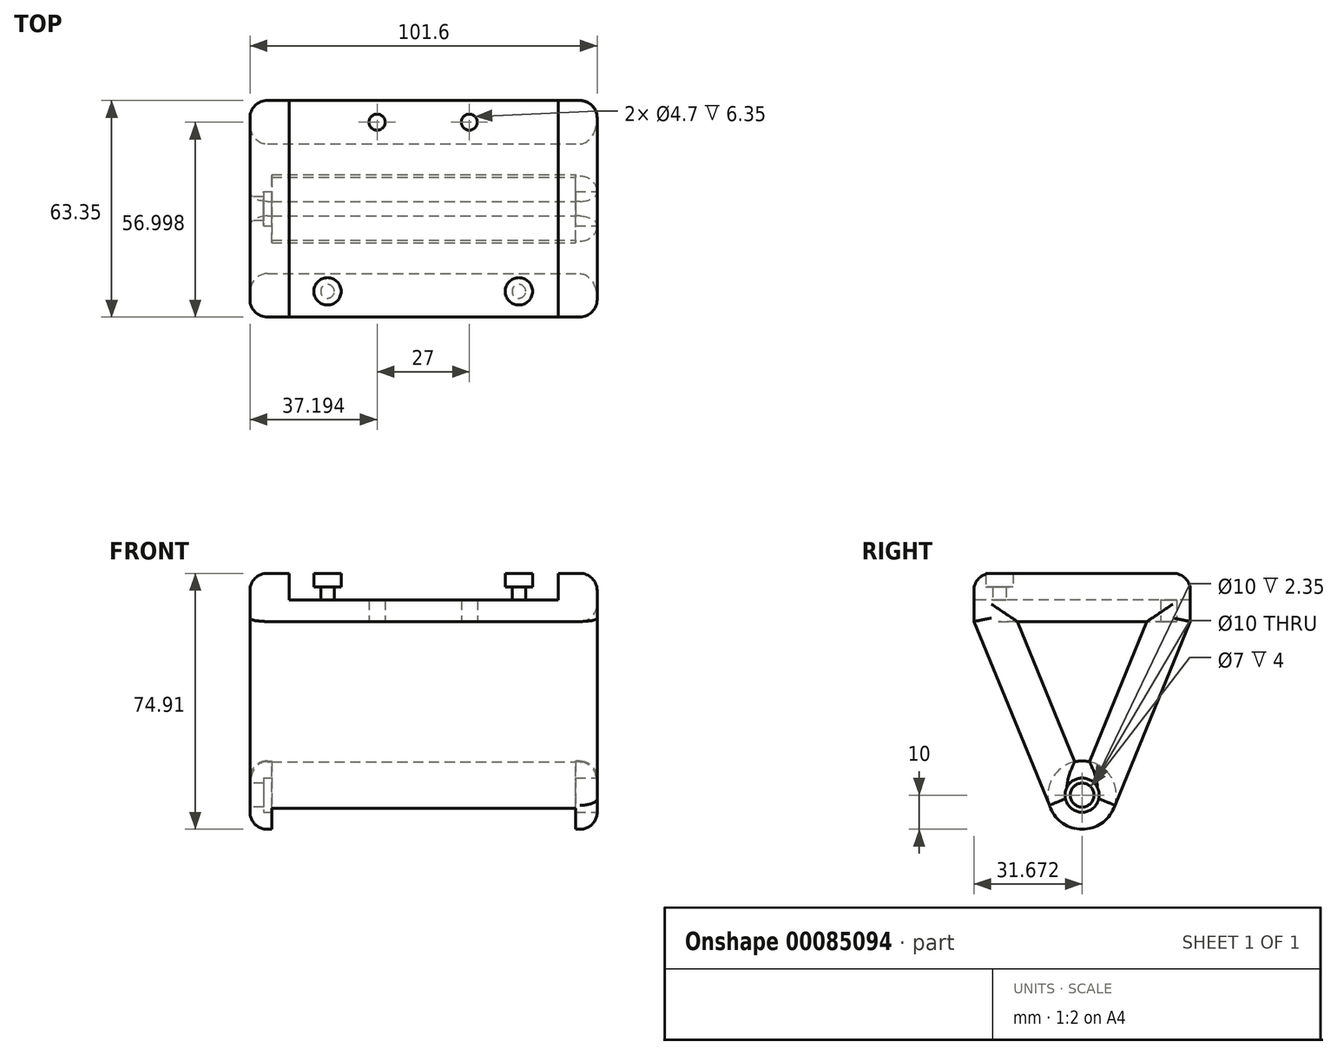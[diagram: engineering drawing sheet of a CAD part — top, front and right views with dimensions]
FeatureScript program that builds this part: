
annotation { "Feature Type Name" : "Feature", "Feature Type Description" : "" }
export const myFeature = defineFeature(function(context is Context, id is Id, definition is map)
    precondition{}
    {
        {
            var Q0;
            Q0=qCreatedBy(makeId("Top.planeOp"),FACE);
            var sketch = newSketch(context, id + "F0", { "sketchPlane" : qUnion([Q0])});
            skLineSegment(sketch, "E0.bottom", {"start": v(-26.44, 29.95) * mm, "end": v(49.76, 29.95) * mm});
            skLineSegment(sketch, "E0.top", {"start": v(-26.44, -27.2) * mm, "end": v(49.76, -27.2) * mm});
            skLineSegment(sketch, "E0.left", {"start": v(-26.44, 29.95) * mm, "end": v(-26.44, -27.2) * mm});
            skLineSegment(sketch, "E0.right", {"start": v(49.76, 29.95) * mm, "end": v(49.76, -27.2) * mm});
            skCircle(sketch, "E1", {"center": v(-16.45, -25.9) * mm, "radius": 2.5 * mm});
            skCircle(sketch, "E2", {"center": v(39.55, -25.9) * mm, "radius": 2.5 * mm});
            skCircle(sketch, "E3", {"center": v(-1.95, 23.6) * mm, "radius": 2.35 * mm});
            skCircle(sketch, "E4", {"center": v(25.05, 23.6) * mm, "radius": 2.35 * mm});
            skLineSegment(sketch, "E5.bottom", {"start": v(3.55, 42.4) * mm, "end": v(19.55, 42.4) * mm});
            skLineSegment(sketch, "E5.top", {"start": v(3.55, 17) * mm, "end": v(19.55, 17) * mm});
            skLineSegment(sketch, "E5.left", {"start": v(3.55, 42.4) * mm, "end": v(3.55, 17) * mm});
            skLineSegment(sketch, "E5.right", {"start": v(19.55, 42.4) * mm, "end": v(19.55, 17) * mm});
            skLineSegment(sketch, "E6.bottom", {"start": v(-18.95, -25.9) * mm, "end": v(-13.95, -25.9) * mm});
            skLineSegment(sketch, "E6.top", {"start": v(-18.95, -27.2) * mm, "end": v(-13.95, -27.2) * mm});
            skLineSegment(sketch, "E6.left", {"start": v(-18.95, -25.9) * mm, "end": v(-18.95, -27.2) * mm});
            skLineSegment(sketch, "E6.right", {"start": v(-13.95, -25.9) * mm, "end": v(-13.95, -27.2) * mm});
            skLineSegment(sketch, "E7.bottom", {"start": v(37.05, -25.9) * mm, "end": v(42.05, -25.9) * mm});
            skLineSegment(sketch, "E7.top", {"start": v(37.05, -27.2) * mm, "end": v(42.05, -27.2) * mm});
            skLineSegment(sketch, "E7.left", {"start": v(37.05, -25.9) * mm, "end": v(37.05, -27.2) * mm});
            skLineSegment(sketch, "E7.right", {"start": v(42.05, -25.9) * mm, "end": v(42.05, -27.2) * mm});
            skLineSegment(sketch, "E8.bottom", {"start": v(-26.44, -27.2) * mm, "end": v(-18.95, -27.2) * mm});
            skLineSegment(sketch, "E8.top", {"start": v(-26.44, -30.2) * mm, "end": v(-18.95, -30.2) * mm});
            skLineSegment(sketch, "E8.left", {"start": v(-26.44, -27.2) * mm, "end": v(-26.44, -30.2) * mm});
            skLineSegment(sketch, "E8.right", {"start": v(-18.95, -27.2) * mm, "end": v(-18.95, -30.2) * mm});
            skLineSegment(sketch, "E9.bottom", {"start": v(49.76, -27.2) * mm, "end": v(42.05, -27.2) * mm});
            skLineSegment(sketch, "E9.top", {"start": v(49.76, -30.2) * mm, "end": v(42.05, -30.2) * mm});
            skLineSegment(sketch, "E9.left", {"start": v(49.76, -27.2) * mm, "end": v(49.76, -30.2) * mm});
            skLineSegment(sketch, "E9.right", {"start": v(42.05, -27.2) * mm, "end": v(42.05, -30.2) * mm});
            skSolve(sketch);
        }
        {
            var Q0;
            Q0=makeQuery(id+"F0.imprint","IMPRINT",FACE,{"disambiguationData":[TD([[makeQuery(id+"F0.imprint","IMPRINT",EDGE,{"derivedFrom":sQuery(id+"F0.wireOp",EDGE,"E0.top")}),1.0]])]});
            var Q1;
            Q1=makeQuery(id+"F0.imprint","IMPRINT",FACE,{"disambiguationData":[TD([[makeQuery(id+"F0.imprint","IMPRINT",EDGE,{"derivedFrom":sQuery(id+"F0.wireOp",EDGE,"E8.bottom")}),-1.0]])]});
            var Q2;
            Q2=makeQuery(id+"F0.imprint","IMPRINT",FACE,{"disambiguationData":[TD([[makeQuery(id+"F0.imprint","IMPRINT",EDGE,{"derivedFrom":sQuery(id+"F0.wireOp",EDGE,"E9.bottom")}),1.0]])]});
            var Q3;
            {var subQ5=sQuery(id+"F0.wireOp",EDGE,"E5.top");Q3=makeQuery(id+"F0.imprint","IMPRINT",FACE,{"disambiguationData":[TD([[makeQuery(id+"F0.imprint","IMPRINT",EDGE,{"derivedFrom":subQ5}),1.0]])]});}
            extrude(context, id + "F1", {"entities" : qUnion([Q0, Q1, Q2, Q3]), "depth" : 6.35 * mm});
        }
        {
            var Q0;
            Q0=makeQuery(id+"F1.opExtrude","CAP_FACE",FACE,{"disambiguationData":[OSD([sQuery(id+"F0.wireOp",EDGE,"E0.bottom"),sQuery(id+"F0.wireOp",EDGE,"E0.top"),sQuery(id+"F0.wireOp",EDGE,"E0.left"),sQuery(id+"F0.wireOp",EDGE,"E0.right"),sQuery(id+"F0.wireOp",EDGE,"E1"),sQuery(id+"F0.wireOp",EDGE,"E2"),sQuery(id+"F0.wireOp",EDGE,"E3"),sQuery(id+"F0.wireOp",EDGE,"E4"),sQuery(id+"F0.wireOp",EDGE,"E5.top"),sQuery(id+"F0.wireOp",EDGE,"E5.left"),sQuery(id+"F0.wireOp",EDGE,"E5.right"),sQuery(id+"F0.wireOp",EDGE,"E6.left"),sQuery(id+"F0.wireOp",EDGE,"E6.right"),sQuery(id+"F0.wireOp",EDGE,"E7.left"),sQuery(id+"F0.wireOp",EDGE,"E7.right"),sQuery(id+"F0.wireOp",EDGE,"E8.top"),sQuery(id+"F0.wireOp",EDGE,"E8.left"),sQuery(id+"F0.wireOp",EDGE,"E8.right"),sQuery(id+"F0.wireOp",EDGE,"E9.top"),sQuery(id+"F0.wireOp",EDGE,"E9.left"),sQuery(id+"F0.wireOp",EDGE,"E9.right")])],"isStart":false});
            var sketch = newSketch(context, id + "F2", { "sketchPlane" : qUnion([Q0])});
            skArc(sketch, "E10.0", {"start": v(-13.95, -25.9) * mm, "mid": v(-16.45, -23.4) * mm, "end": v(-18.95, -25.9) * mm});
            skArc(sketch, "E11.0", {"start": v(42.05, -25.9) * mm, "mid": v(39.55, -23.4) * mm, "end": v(37.05, -25.9) * mm});
            skCircle(sketch, "E12", {"center": v(-16.45, -25.9) * mm, "radius": 7.5 * mm});
            skCircle(sketch, "E13", {"center": v(39.55, -25.9) * mm, "radius": 7.5 * mm});
            skLineSegment(sketch, "E14.bottom", {"start": v(-23.95, -25.9) * mm, "end": v(47.05, -25.9) * mm});
            skLineSegment(sketch, "E14.top", {"start": v(-23.95, -33.4) * mm, "end": v(47.05, -33.4) * mm});
            skLineSegment(sketch, "E14.left", {"start": v(-23.95, -25.9) * mm, "end": v(-23.95, -33.4) * mm});
            skLineSegment(sketch, "E14.right", {"start": v(47.05, -25.9) * mm, "end": v(47.05, -33.4) * mm});
            skLineSegment(sketch, "E15.bottom", {"start": v(-23.95, -25.9) * mm, "end": v(-8.95, -25.9) * mm});
            skLineSegment(sketch, "E15.top", {"start": v(-23.95, -33.4) * mm, "end": v(-8.95, -33.4) * mm});
            skLineSegment(sketch, "E15.right", {"start": v(-8.95, -25.9) * mm, "end": v(-8.95, -33.4) * mm});
            skLineSegment(sketch, "E16.bottom", {"start": v(47.05, -25.9) * mm, "end": v(32.05, -25.9) * mm});
            skLineSegment(sketch, "E16.top", {"start": v(47.05, -33.4) * mm, "end": v(32.05, -33.4) * mm});
            skLineSegment(sketch, "E16.right", {"start": v(32.05, -25.9) * mm, "end": v(32.05, -33.4) * mm});
            skLineSegment(sketch, "E17.bottom", {"start": v(-26.44, -25.12) * mm, "end": v(49.76, -25.12) * mm});
            skLineSegment(sketch, "E17.top", {"start": v(-26.44, -33.4) * mm, "end": v(49.76, -33.4) * mm});
            skLineSegment(sketch, "E17.left", {"start": v(-26.44, -25.12) * mm, "end": v(-26.44, -33.4) * mm});
            skLineSegment(sketch, "E17.right", {"start": v(49.76, -25.12) * mm, "end": v(49.76, -33.4) * mm});
            skSolve(sketch);
        }
        {
            var Q0;
            {var subQ1=sQuery(id+"F2.wireOp",EDGE,"E13");var subQ3=sQuery(id+"F0.wireOp",EDGE,"E9.top");var subQ4=makeQuery(id+"F1.opExtrude","CAP_EDGE",EDGE,{"disambiguationData":[OSD([subQ3])],"isStart":false});var subQ5=makeQuery(id+"F2.imprint","INTERSECT",VERTEX,{"derivedFrom":[subQ4,subQ1]});Q0=makeQuery(id+"F2.imprint","IMPRINT",FACE,{"disambiguationData":[TD([[makeQuery(id+"F2.imprint","IMPRINT",EDGE,{"disambiguationData":[TD([[subQ5,-1.0]])],"derivedFrom":subQ1}),-1.0]])]});}
            var Q1;
            {var subQ0=sQuery(id+"F2.wireOp",EDGE,"E10.0");Q1=makeQuery(id+"F2.imprint","IMPRINT",FACE,{"disambiguationData":[TD([[makeQuery(id+"F2.imprint","IMPRINT",EDGE,{"derivedFrom":subQ0}),-1.0]])]});}
            var Q2;
            {var subQ0=sQuery(id+"F2.wireOp",EDGE,"E11.0");Q2=makeQuery(id+"F2.imprint","IMPRINT",FACE,{"disambiguationData":[TD([[makeQuery(id+"F2.imprint","IMPRINT",EDGE,{"derivedFrom":subQ0}),-1.0]])]});}
            var Q3;
            {var subQ5=makeQuery(id+"F1.opExtrude","CAP_EDGE",EDGE,{"disambiguationData":[OSD([sQuery(id+"F0.wireOp",EDGE,"E6.left"),sQuery(id+"F0.wireOp",EDGE,"E8.right")])],"isStart":false});Q3=makeQuery(id+"F2.imprint","IMPRINT",FACE,{"disambiguationData":[TD([[makeQuery(id+"F2.imprint","IMPRINT",EDGE,{"derivedFrom":subQ5}),-1.0]])]});}
            var Q4;
            {var subQ5=makeQuery(id+"F1.opExtrude","CAP_EDGE",EDGE,{"disambiguationData":[OSD([sQuery(id+"F0.wireOp",EDGE,"E6.right")])],"isStart":false});Q4=makeQuery(id+"F2.imprint","IMPRINT",FACE,{"disambiguationData":[TD([[makeQuery(id+"F2.imprint","IMPRINT",EDGE,{"derivedFrom":subQ5}),1.0]])]});}
            var Q5;
            {var subQ5=makeQuery(id+"F1.opExtrude","CAP_EDGE",EDGE,{"disambiguationData":[OSD([sQuery(id+"F0.wireOp",EDGE,"E7.left")])],"isStart":false});Q5=makeQuery(id+"F2.imprint","IMPRINT",FACE,{"disambiguationData":[TD([[makeQuery(id+"F2.imprint","IMPRINT",EDGE,{"derivedFrom":subQ5}),-1.0]])]});}
            var Q6;
            {var subQ5=makeQuery(id+"F1.opExtrude","CAP_EDGE",EDGE,{"disambiguationData":[OSD([sQuery(id+"F0.wireOp",EDGE,"E7.right"),sQuery(id+"F0.wireOp",EDGE,"E9.right")])],"isStart":false});Q6=makeQuery(id+"F2.imprint","IMPRINT",FACE,{"disambiguationData":[TD([[makeQuery(id+"F2.imprint","IMPRINT",EDGE,{"derivedFrom":subQ5}),1.0]])]});}
            var Q7;
            {var subQ0=sQuery(id+"F2.wireOp",EDGE,"E15.top");var subQ1=sQuery(id+"F2.wireOp",EDGE,"E12");var subQ2=makeQuery(id+"F2.imprint","INTERSECT",VERTEX,{"derivedFrom":[subQ1,subQ0]});Q7=makeQuery(id+"F2.imprint","IMPRINT",FACE,{"disambiguationData":[TD([[makeQuery(id+"F2.imprint","IMPRINT",EDGE,{"disambiguationData":[TD([[subQ2,-1.0]])],"derivedFrom":subQ1}),-1.0]])]});}
            var Q8;
            {var subQ1=sQuery(id+"F2.wireOp",EDGE,"E12");var subQ3=sQuery(id+"F0.wireOp",EDGE,"E8.top");var subQ4=makeQuery(id+"F1.opExtrude","CAP_EDGE",EDGE,{"disambiguationData":[OSD([subQ3])],"isStart":false});var subQ5=makeQuery(id+"F2.imprint","INTERSECT",VERTEX,{"derivedFrom":[subQ4,subQ1]});Q8=makeQuery(id+"F2.imprint","IMPRINT",FACE,{"disambiguationData":[TD([[makeQuery(id+"F2.imprint","IMPRINT",EDGE,{"disambiguationData":[TD([[subQ5,1.0]])],"derivedFrom":subQ1}),-1.0]])]});}
            var Q9;
            {var subQ1=sQuery(id+"F2.wireOp",EDGE,"E12");var subQ3=sQuery(id+"F0.wireOp",EDGE,"E8.top");var subQ4=makeQuery(id+"F1.opExtrude","CAP_EDGE",EDGE,{"disambiguationData":[OSD([subQ3])],"isStart":false});var subQ5=makeQuery(id+"F2.imprint","INTERSECT",VERTEX,{"derivedFrom":[subQ4,subQ1]});Q9=makeQuery(id+"F2.imprint","IMPRINT",FACE,{"disambiguationData":[TD([[makeQuery(id+"F2.imprint","IMPRINT",EDGE,{"disambiguationData":[TD([[subQ5,1.0]])],"derivedFrom":subQ1}),-1.0]])]});}
            var Q10;
            {var subQ1=sQuery(id+"F2.wireOp",EDGE,"E13");var subQ3=sQuery(id+"F0.wireOp",EDGE,"E9.top");var subQ4=makeQuery(id+"F1.opExtrude","CAP_EDGE",EDGE,{"disambiguationData":[OSD([subQ3])],"isStart":false});var subQ5=makeQuery(id+"F2.imprint","INTERSECT",VERTEX,{"derivedFrom":[subQ4,subQ1]});Q10=makeQuery(id+"F2.imprint","IMPRINT",FACE,{"disambiguationData":[TD([[makeQuery(id+"F2.imprint","IMPRINT",EDGE,{"disambiguationData":[TD([[subQ5,-1.0]])],"derivedFrom":subQ1}),-1.0]])]});}
            var Q11;
            {var subQ0=makeQuery(id+"F1.opExtrude","CAP_EDGE",EDGE,{"disambiguationData":[OSD([sQuery(id+"F0.wireOp",EDGE,"E7.left")])],"isStart":false});Q11=makeQuery(id+"F2.imprint","IMPRINT",FACE,{"disambiguationData":[TD([[makeQuery(id+"F2.imprint","IMPRINT",EDGE,{"derivedFrom":subQ0}),1.0]])]});}
            var Q12;
            {var subQ0=sQuery(id+"F2.wireOp",EDGE,"E16.top");var subQ1=sQuery(id+"F2.wireOp",EDGE,"E13");var subQ2=makeQuery(id+"F2.imprint","INTERSECT",VERTEX,{"derivedFrom":[subQ1,subQ0]});Q12=makeQuery(id+"F2.imprint","IMPRINT",FACE,{"disambiguationData":[TD([[makeQuery(id+"F2.imprint","IMPRINT",EDGE,{"disambiguationData":[TD([[subQ2,1.0]])],"derivedFrom":subQ1}),-1.0]])]});}
            var Q13;
            {var subQ1=sQuery(id+"F2.wireOp",EDGE,"E13");var subQ3=makeQuery(id+"F1.opExtrude","CAP_EDGE",EDGE,{"disambiguationData":[OSD([sQuery(id+"F0.wireOp",EDGE,"E0.top")])],"isStart":false});var subQ4=makeQuery(id+"F2.imprint","INTERSECT",VERTEX,{"derivedFrom":[subQ3,subQ1]});Q13=makeQuery(id+"F2.imprint","IMPRINT",FACE,{"disambiguationData":[TD([[makeQuery(id+"F2.imprint","IMPRINT",EDGE,{"disambiguationData":[TD([[subQ4,1.0]])],"derivedFrom":subQ3}),1.0]])]});}
            var Q14;
            {var subQ1=sQuery(id+"F2.wireOp",EDGE,"E12");var subQ3=makeQuery(id+"F1.opExtrude","CAP_EDGE",EDGE,{"disambiguationData":[OSD([sQuery(id+"F0.wireOp",EDGE,"E0.top")])],"isStart":false});var subQ4=makeQuery(id+"F2.imprint","INTERSECT",VERTEX,{"derivedFrom":[subQ3,subQ1]});Q14=makeQuery(id+"F2.imprint","IMPRINT",FACE,{"disambiguationData":[TD([[makeQuery(id+"F2.imprint","IMPRINT",EDGE,{"disambiguationData":[TD([[subQ4,-1.0]])],"derivedFrom":subQ3}),1.0]])]});}
            var Q15;
            {var subQ0=sQuery(id+"F2.wireOp",EDGE,"E15.top");var subQ7=sQuery(id+"F2.wireOp",EDGE,"E14.left");var subQ8=makeQuery(id+"F2.imprint","INTERSECT",VERTEX,{"derivedFrom":[subQ0,subQ7]});Q15=makeQuery(id+"F2.imprint","IMPRINT",FACE,{"disambiguationData":[TD([[makeQuery(id+"F2.imprint","IMPRINT",EDGE,{"disambiguationData":[TD([[subQ8,-1.0]])],"derivedFrom":subQ0}),1.0]])]});}
            var Q16;
            {var subQ5=sQuery(id+"F0.wireOp",EDGE,"E6.right");var subQ6=makeQuery(id+"F1.opExtrude","CAP_EDGE",EDGE,{"disambiguationData":[OSD([subQ5])],"isStart":false});Q16=makeQuery(id+"F2.imprint","IMPRINT",FACE,{"disambiguationData":[TD([[makeQuery(id+"F2.imprint","IMPRINT",EDGE,{"derivedFrom":subQ6}),-1.0]])]});}
            var Q17;
            {var subQ0=sQuery(id+"F2.wireOp",EDGE,"E10.0");Q17=makeQuery(id+"F2.imprint","IMPRINT",FACE,{"disambiguationData":[TD([[makeQuery(id+"F2.imprint","IMPRINT",EDGE,{"derivedFrom":subQ0}),1.0]])]});}
            var Q18;
            {var subQ0=sQuery(id+"F2.wireOp",EDGE,"E14.top");Q18=makeQuery(id+"F2.imprint","IMPRINT",FACE,{"disambiguationData":[TD([[makeQuery(id+"F2.imprint","IMPRINT",EDGE,{"derivedFrom":subQ0}),1.0]])]});}
            var Q19;
            {var subQ0=sQuery(id+"F2.wireOp",EDGE,"E11.0");Q19=makeQuery(id+"F2.imprint","IMPRINT",FACE,{"disambiguationData":[TD([[makeQuery(id+"F2.imprint","IMPRINT",EDGE,{"derivedFrom":subQ0}),1.0]])]});}
            var Q20;
            {var subQ0=sQuery(id+"F2.wireOp",EDGE,"E16.top");var subQ7=sQuery(id+"F2.wireOp",EDGE,"E14.right");var subQ8=makeQuery(id+"F2.imprint","INTERSECT",VERTEX,{"derivedFrom":[subQ0,subQ7]});Q20=makeQuery(id+"F2.imprint","IMPRINT",FACE,{"disambiguationData":[TD([[makeQuery(id+"F2.imprint","IMPRINT",EDGE,{"disambiguationData":[TD([[subQ8,-1.0]])],"derivedFrom":subQ0}),-1.0]])]});}
            var Q21;
            {var subQ8=sQuery(id+"F2.wireOp",EDGE,"E17.left");Q21=makeQuery(id+"F2.imprint","IMPRINT",FACE,{"disambiguationData":[TD([[makeQuery(id+"F2.imprint","IMPRINT",EDGE,{"derivedFrom":subQ8}),1.0]])]});}
            var Q22;
            {var subQ0=sQuery(id+"F2.wireOp",EDGE,"E17.top");var subQ1=sQuery(id+"F2.wireOp",EDGE,"E15.right");var subQ2=makeQuery(id+"F2.imprint","INTERSECT",VERTEX,{"derivedFrom":[subQ1,subQ0]});Q22=makeQuery(id+"F2.imprint","IMPRINT",FACE,{"disambiguationData":[TD([[makeQuery(id+"F2.imprint","IMPRINT",EDGE,{"disambiguationData":[TD([[subQ2,1.0]])],"derivedFrom":subQ1}),1.0]])]});}
            var Q23;
            {var subQ0=sQuery(id+"F2.wireOp",EDGE,"E17.top");var subQ1=sQuery(id+"F2.wireOp",EDGE,"E12");var subQ2=makeQuery(id+"F2.imprint","INTERSECT",VERTEX,{"derivedFrom":[subQ1,subQ0]});Q23=makeQuery(id+"F2.imprint","IMPRINT",FACE,{"disambiguationData":[TD([[makeQuery(id+"F2.imprint","IMPRINT",EDGE,{"disambiguationData":[TD([[subQ2,-1.0]])],"derivedFrom":subQ1}),-1.0]])]});}
            var Q24;
            {var subQ0=sQuery(id+"F2.wireOp",EDGE,"E17.top");var subQ7=sQuery(id+"F2.wireOp",EDGE,"E14.left");var subQ8=makeQuery(id+"F2.imprint","INTERSECT",VERTEX,{"derivedFrom":[subQ7,subQ0]});Q24=makeQuery(id+"F2.imprint","IMPRINT",FACE,{"disambiguationData":[TD([[makeQuery(id+"F2.imprint","IMPRINT",EDGE,{"disambiguationData":[TD([[subQ8,-1.0]])],"derivedFrom":subQ0}),1.0]])]});}
            var Q25;
            {var subQ0=sQuery(id+"F2.wireOp",EDGE,"E17.bottom");var subQ1=sQuery(id+"F2.wireOp",EDGE,"E10.0");var subQ2=makeQuery(id+"F2.imprint","INTERSECT",VERTEX,{"disambiguationData":[OD(0.0)],"derivedFrom":[subQ1,subQ0]});Q25=makeQuery(id+"F2.imprint","IMPRINT",FACE,{"disambiguationData":[TD([[makeQuery(id+"F2.imprint","IMPRINT",EDGE,{"disambiguationData":[TD([[subQ2,-1.0]])],"derivedFrom":subQ1}),1.0]])]});}
            var Q26;
            {var subQ0=sQuery(id+"F2.wireOp",EDGE,"E17.top");var subQ1=sQuery(id+"F2.wireOp",EDGE,"E13");var subQ2=makeQuery(id+"F2.imprint","INTERSECT",VERTEX,{"derivedFrom":[subQ1,subQ0]});Q26=makeQuery(id+"F2.imprint","IMPRINT",FACE,{"disambiguationData":[TD([[makeQuery(id+"F2.imprint","IMPRINT",EDGE,{"disambiguationData":[TD([[subQ2,1.0]])],"derivedFrom":subQ1}),-1.0]])]});}
            var Q27;
            {var subQ0=sQuery(id+"F2.wireOp",EDGE,"E17.top");var subQ7=sQuery(id+"F2.wireOp",EDGE,"E14.right");var subQ8=makeQuery(id+"F2.imprint","INTERSECT",VERTEX,{"derivedFrom":[subQ7,subQ0]});Q27=makeQuery(id+"F2.imprint","IMPRINT",FACE,{"disambiguationData":[TD([[makeQuery(id+"F2.imprint","IMPRINT",EDGE,{"disambiguationData":[TD([[subQ8,1.0]])],"derivedFrom":subQ0}),1.0]])]});}
            var Q28;
            {var subQ8=sQuery(id+"F2.wireOp",EDGE,"E17.right");Q28=makeQuery(id+"F2.imprint","IMPRINT",FACE,{"disambiguationData":[TD([[makeQuery(id+"F2.imprint","IMPRINT",EDGE,{"derivedFrom":subQ8}),-1.0]])]});}
            var Q29;
            {var subQ0=sQuery(id+"F2.wireOp",EDGE,"E17.bottom");var subQ1=sQuery(id+"F2.wireOp",EDGE,"E11.0");var subQ2=makeQuery(id+"F2.imprint","INTERSECT",VERTEX,{"disambiguationData":[OD(0.0)],"derivedFrom":[subQ1,subQ0]});Q29=makeQuery(id+"F2.imprint","IMPRINT",FACE,{"disambiguationData":[TD([[makeQuery(id+"F2.imprint","IMPRINT",EDGE,{"disambiguationData":[TD([[subQ2,-1.0]])],"derivedFrom":subQ1}),1.0]])]});}
            var Q30;
            Q30=makeQuery(id+"F1.opExtrude","CAP_FACE",FACE,{"disambiguationData":[OSD([sQuery(id+"F0.wireOp",EDGE,"E0.bottom"),sQuery(id+"F0.wireOp",EDGE,"E0.top"),sQuery(id+"F0.wireOp",EDGE,"E0.left"),sQuery(id+"F0.wireOp",EDGE,"E0.right"),sQuery(id+"F0.wireOp",EDGE,"E1"),sQuery(id+"F0.wireOp",EDGE,"E2"),sQuery(id+"F0.wireOp",EDGE,"E3"),sQuery(id+"F0.wireOp",EDGE,"E4"),sQuery(id+"F0.wireOp",EDGE,"E5.top"),sQuery(id+"F0.wireOp",EDGE,"E5.left"),sQuery(id+"F0.wireOp",EDGE,"E5.right"),sQuery(id+"F0.wireOp",EDGE,"E6.left"),sQuery(id+"F0.wireOp",EDGE,"E6.right"),sQuery(id+"F0.wireOp",EDGE,"E7.left"),sQuery(id+"F0.wireOp",EDGE,"E7.right"),sQuery(id+"F0.wireOp",EDGE,"E8.top"),sQuery(id+"F0.wireOp",EDGE,"E8.left"),sQuery(id+"F0.wireOp",EDGE,"E8.right"),sQuery(id+"F0.wireOp",EDGE,"E9.top"),sQuery(id+"F0.wireOp",EDGE,"E9.left"),sQuery(id+"F0.wireOp",EDGE,"E9.right")])],"isStart":true});
            extrude(context, id + "F3", {"entities" : qUnion([Q0, Q1, Q2, Q3, Q4, Q5, Q6, Q7, Q8, Q9, Q10, Q11, Q12, Q13, Q14, Q15, Q16, Q17, Q18, Q19, Q20, Q21, Q22, Q23, Q24, Q25, Q26, Q27, Q28, Q29]), "operationType" : NewBodyOperationType.ADD, "endBound" : BoundingType.UP_TO_SURFACE, "oppositeDirection" : true, "endBoundEntityFace" : qUnion([Q30]), "depth" : 6.35 * mm - 3.75 * mm});
        }
        {
            var Q0;
            Q0=makeQuery(id+"F1.opExtrude","CAP_FACE",FACE,{"disambiguationData":[OSD([sQuery(id+"F0.wireOp",EDGE,"E0.bottom"),sQuery(id+"F0.wireOp",EDGE,"E0.top"),sQuery(id+"F0.wireOp",EDGE,"E0.left"),sQuery(id+"F0.wireOp",EDGE,"E0.right"),sQuery(id+"F0.wireOp",EDGE,"E1"),sQuery(id+"F0.wireOp",EDGE,"E2"),sQuery(id+"F0.wireOp",EDGE,"E3"),sQuery(id+"F0.wireOp",EDGE,"E4"),sQuery(id+"F0.wireOp",EDGE,"E6.left"),sQuery(id+"F0.wireOp",EDGE,"E6.right"),sQuery(id+"F0.wireOp",EDGE,"E7.left"),sQuery(id+"F0.wireOp",EDGE,"E7.right"),sQuery(id+"F0.wireOp",EDGE,"E8.top"),sQuery(id+"F0.wireOp",EDGE,"E8.left"),sQuery(id+"F0.wireOp",EDGE,"E8.right"),sQuery(id+"F0.wireOp",EDGE,"E9.top"),sQuery(id+"F0.wireOp",EDGE,"E9.left"),sQuery(id+"F0.wireOp",EDGE,"E9.right")])],"isStart":false});
            var sketch = newSketch(context, id + "F4", { "sketchPlane" : qUnion([Q0])});
            skArc(sketch, "E18.0.0", {"start": v(32.05, -25.9) * mm, "mid": v(39.55, -18.4) * mm, "end": v(47.05, -25.9) * mm});
            skLineSegment(sketch, "E18.0.1", {"start": v(47.05, -25.9) * mm, "end": v(47.05, -29.61) * mm});
            skArc(sketch, "E18.0.2", {"start": v(47.05, -29.61) * mm, "mid": v(49.03, -27.74) * mm, "end": v(49.76, -25.12) * mm});
            skLineSegment(sketch, "E18.0.3", {"start": v(49.76, -25.12) * mm, "end": v(49.76, 24.87) * mm});
            skArc(sketch, "E18.0.4", {"start": v(49.76, 24.87) * mm, "mid": v(48.27, 28.46) * mm, "end": v(44.68, 29.95) * mm});
            skLineSegment(sketch, "E18.0.5", {"start": v(44.68, 29.95) * mm, "end": v(-21.36, 29.95) * mm});
            skArc(sketch, "E18.0.6", {"start": v(-21.36, 29.95) * mm, "mid": v(-24.95, 28.46) * mm, "end": v(-26.44, 24.87) * mm});
            skLineSegment(sketch, "E18.0.7", {"start": v(-26.44, 24.87) * mm, "end": v(-26.44, -25.12) * mm});
            skArc(sketch, "E18.0.8", {"start": v(-26.44, -25.12) * mm, "mid": v(-25.77, -27.64) * mm, "end": v(-23.95, -29.5) * mm});
            skLineSegment(sketch, "E18.0.9", {"start": v(-23.95, -29.5) * mm, "end": v(-23.95, -25.9) * mm});
            skArc(sketch, "E18.0.10", {"start": v(-23.95, -25.9) * mm, "mid": v(-16.45, -18.4) * mm, "end": v(-8.95, -25.9) * mm});
            skLineSegment(sketch, "E18.0.11", {"start": v(-8.95, -25.9) * mm, "end": v(-8.95, -27.2) * mm});
            skLineSegment(sketch, "E18.0.12", {"start": v(-8.95, -27.2) * mm, "end": v(32.05, -27.2) * mm});
            skLineSegment(sketch, "E18.0.13", {"start": v(32.05, -27.2) * mm, "end": v(32.05, -25.9) * mm});
            skLineSegment(sketch, "E19.0.0", {"start": v(-13.95, -27.2) * mm, "end": v(-8.95, -27.2) * mm});
            skLineSegment(sketch, "E19.0.1", {"start": v(-8.95, -27.2) * mm, "end": v(-8.95, -25.9) * mm});
            skArc(sketch, "E19.0.2", {"start": v(-8.95, -25.9) * mm, "mid": v(-16.45, -18.4) * mm, "end": v(-23.95, -25.9) * mm});
            skLineSegment(sketch, "E19.0.3", {"start": v(-23.95, -25.9) * mm, "end": v(-23.95, -29.5) * mm});
            skArc(sketch, "E19.0.4", {"start": v(-21.36, -30.2) * mm, "mid": v(-22.7, -30.02) * mm, "end": v(-23.95, -29.5) * mm});
            skLineSegment(sketch, "E19.0.5", {"start": v(-21.36, -30.2) * mm, "end": v(-18.95, -30.2) * mm});
            skLineSegment(sketch, "E19.0.6", {"start": v(-18.95, -30.2) * mm, "end": v(-18.95, -25.9) * mm});
            skArc(sketch, "E19.0.7", {"start": v(-18.95, -25.9) * mm, "mid": v(-16.45, -23.4) * mm, "end": v(-13.95, -25.9) * mm});
            skLineSegment(sketch, "E19.0.8", {"start": v(-13.95, -25.9) * mm, "end": v(-13.95, -27.2) * mm});
            skLineSegment(sketch, "E20.0.0", {"start": v(32.05, -27.2) * mm, "end": v(37.05, -27.2) * mm});
            skLineSegment(sketch, "E20.0.1", {"start": v(37.05, -27.2) * mm, "end": v(37.05, -25.9) * mm});
            skArc(sketch, "E20.0.2", {"start": v(37.05, -25.9) * mm, "mid": v(39.55, -23.4) * mm, "end": v(42.05, -25.9) * mm});
            skLineSegment(sketch, "E20.0.3", {"start": v(42.05, -25.9) * mm, "end": v(42.05, -30.2) * mm});
            skLineSegment(sketch, "E20.0.4", {"start": v(42.05, -30.2) * mm, "end": v(44.68, -30.2) * mm});
            skArc(sketch, "E20.0.5", {"start": v(47.05, -29.61) * mm, "mid": v(45.9, -30.05) * mm, "end": v(44.68, -30.2) * mm});
            skLineSegment(sketch, "E20.0.6", {"start": v(47.05, -29.61) * mm, "end": v(47.05, -25.9) * mm});
            skArc(sketch, "E20.0.7", {"start": v(47.05, -25.9) * mm, "mid": v(39.55, -18.4) * mm, "end": v(32.05, -25.9) * mm});
            skLineSegment(sketch, "E20.0.8", {"start": v(32.05, -25.9) * mm, "end": v(32.05, -27.2) * mm});
            skLineSegment(sketch, "E21.bottom", {"start": v(-18.95, -30.2) * mm, "end": v(42.05, -30.2) * mm});
            skLineSegment(sketch, "E21.top", {"start": v(-18.95, -27.2) * mm, "end": v(42.05, -27.2) * mm});
            skLineSegment(sketch, "E21.left", {"start": v(-18.95, -30.2) * mm, "end": v(-18.95, -27.2) * mm});
            skLineSegment(sketch, "E21.right", {"start": v(42.05, -30.2) * mm, "end": v(42.05, -27.2) * mm});
            skCircle(sketch, "E22", {"center": v(-16.45, -25.9) * mm, "radius": 2.5 * mm});
            skCircle(sketch, "E23", {"center": v(-16.45, -25.9) * mm, "radius": 7.5 * mm});
            skCircle(sketch, "E24", {"center": v(39.55, -25.9) * mm, "radius": 2.5 * mm});
            skCircle(sketch, "E25", {"center": v(39.55, -25.9) * mm, "radius": 7.5 * mm});
            skCircle(sketch, "E26", {"center": v(39.55, -25.9) * mm, "radius": 2 * mm});
            skCircle(sketch, "E27", {"center": v(39.55, -25.9) * mm, "radius": 4 * mm});
            skCircle(sketch, "E28", {"center": v(-16.45, -25.9) * mm, "radius": 2 * mm});
            skCircle(sketch, "E29", {"center": v(-16.45, -25.9) * mm, "radius": 4 * mm});
            skSolve(sketch);
        }
        {
            var Q0;
            {var subQ0=sQuery(id+"F4.wireOp",EDGE,"E28");var subQ1=sQuery(id+"F4.wireOp",EDGE,"E21.top");var subQ2=makeQuery(id+"F4.imprint","INTERSECT",VERTEX,{"disambiguationData":[OD(0.0)],"derivedFrom":[subQ1,subQ0]});Q0=makeQuery(id+"F4.imprint","IMPRINT",FACE,{"disambiguationData":[TD([[makeQuery(id+"F4.imprint","IMPRINT",EDGE,{"disambiguationData":[TD([[subQ2,-1.0]])],"derivedFrom":subQ1}),1.0]])]});}
            var Q1;
            {var subQ0=sQuery(id+"F4.wireOp",EDGE,"E28");var subQ1=sQuery(id+"F4.wireOp",EDGE,"E21.top");var subQ2=makeQuery(id+"F4.imprint","INTERSECT",VERTEX,{"disambiguationData":[OD(0.0)],"derivedFrom":[subQ1,subQ0]});Q1=makeQuery(id+"F4.imprint","IMPRINT",FACE,{"disambiguationData":[TD([[makeQuery(id+"F4.imprint","IMPRINT",EDGE,{"disambiguationData":[TD([[subQ2,-1.0]])],"derivedFrom":subQ1}),-1.0]])]});}
            var Q2;
            {var subQ0=sQuery(id+"F4.wireOp",EDGE,"E26");var subQ1=sQuery(id+"F4.wireOp",EDGE,"E21.top");var subQ2=makeQuery(id+"F4.imprint","INTERSECT",VERTEX,{"disambiguationData":[OD(0.0)],"derivedFrom":[subQ1,subQ0]});Q2=makeQuery(id+"F4.imprint","IMPRINT",FACE,{"disambiguationData":[TD([[makeQuery(id+"F4.imprint","IMPRINT",EDGE,{"disambiguationData":[TD([[subQ2,-1.0]])],"derivedFrom":subQ1}),1.0]])]});}
            var Q3;
            {var subQ0=sQuery(id+"F4.wireOp",EDGE,"E26");var subQ1=sQuery(id+"F4.wireOp",EDGE,"E21.top");var subQ2=makeQuery(id+"F4.imprint","INTERSECT",VERTEX,{"disambiguationData":[OD(0.0)],"derivedFrom":[subQ1,subQ0]});Q3=makeQuery(id+"F4.imprint","IMPRINT",FACE,{"disambiguationData":[TD([[makeQuery(id+"F4.imprint","IMPRINT",EDGE,{"disambiguationData":[TD([[subQ2,-1.0]])],"derivedFrom":subQ1}),-1.0]])]});}
            extrude(context, id + "F5", {"entities" : qUnion([Q0, Q1, Q2, Q3]), "operationType" : NewBodyOperationType.ADD, "depth" : 3.76 * mm});
        }
        {
            var Q0;
            Q0=makeQuery(id+"F5.opExtrude","CAP_FACE",FACE,{"disambiguationData":[OSD([sQuery(id+"F4.wireOp",EDGE,"E28")])],"isStart":false});
            var sketch = newSketch(context, id + "F6", { "sketchPlane" : qUnion([Q0])});
            skCircle(sketch, "E30.0.0", {"center": v(-16.45, -25.9) * mm, "radius": 2 * mm});
            skCircle(sketch, "E31.0.0", {"center": v(39.55, -25.9) * mm, "radius": 2 * mm});
            skCircle(sketch, "E32", {"center": v(-16.45, -25.9) * mm, "radius": 4 * mm});
            skCircle(sketch, "E33", {"center": v(39.55, -25.9) * mm, "radius": 4 * mm});
            skSolve(sketch);
        }
        {
            var Q0;
            Q0=makeQuery(id+"F6.imprint","IMPRINT",FACE,{"disambiguationData":[TD([[makeQuery(id+"F6.imprint","IMPRINT",EDGE,{"derivedFrom":sQuery(id+"F6.wireOp",EDGE,"E30.0.0")}),-1.0]])]});
            var Q1;
            Q1=makeQuery(id+"F6.imprint","IMPRINT",FACE,{"disambiguationData":[TD([[makeQuery(id+"F6.imprint","IMPRINT",EDGE,{"derivedFrom":sQuery(id+"F6.wireOp",EDGE,"E30.0.0")}),1.0]])]});
            var Q2;
            Q2=makeQuery(id+"F6.imprint","IMPRINT",FACE,{"disambiguationData":[TD([[makeQuery(id+"F6.imprint","IMPRINT",EDGE,{"derivedFrom":sQuery(id+"F6.wireOp",EDGE,"E31.0.0")}),-1.0]])]});
            var Q3;
            Q3=makeQuery(id+"F6.imprint","IMPRINT",FACE,{"disambiguationData":[TD([[makeQuery(id+"F6.imprint","IMPRINT",EDGE,{"derivedFrom":sQuery(id+"F6.wireOp",EDGE,"E31.0.0")}),1.0]])]});
            extrude(context, id + "F7", {"entities" : qUnion([Q0, Q1, Q2, Q3]), "operationType" : NewBodyOperationType.ADD, "depth" : 4 * mm});
        }
        {
            var Q0;
            {var subQ0=sQuery(id+"F0.wireOp",EDGE,"E9.right");var subQ1=sQuery(id+"F0.wireOp",EDGE,"E9.left");var subQ2=sQuery(id+"F0.wireOp",EDGE,"E9.top");var subQ3=sQuery(id+"F0.wireOp",EDGE,"E8.right");var subQ4=sQuery(id+"F0.wireOp",EDGE,"E8.left");var subQ5=sQuery(id+"F0.wireOp",EDGE,"E8.top");var subQ6=sQuery(id+"F0.wireOp",EDGE,"E7.right");var subQ7=sQuery(id+"F0.wireOp",EDGE,"E7.left");var subQ8=sQuery(id+"F0.wireOp",EDGE,"E6.right");var subQ9=sQuery(id+"F0.wireOp",EDGE,"E6.left");var subQ10=sQuery(id+"F0.wireOp",EDGE,"E4");var subQ11=sQuery(id+"F0.wireOp",EDGE,"E3");var subQ12=sQuery(id+"F0.wireOp",EDGE,"E2");var subQ13=sQuery(id+"F0.wireOp",EDGE,"E1");var subQ14=sQuery(id+"F0.wireOp",EDGE,"E0.right");var subQ15=sQuery(id+"F0.wireOp",EDGE,"E0.left");var subQ16=sQuery(id+"F0.wireOp",EDGE,"E0.top");var subQ17=sQuery(id+"F0.wireOp",EDGE,"E0.bottom");Q0=makeQuery(id+"F3.boolean.opBoolean","MERGE",FACE,{"derivedFrom":[makeQuery(id+"F1.opExtrude","CAP_FACE",FACE,{"disambiguationData":[OSD([subQ17,subQ16,subQ15,subQ14,subQ13,subQ12,subQ11,subQ10,subQ9,subQ8,subQ7,subQ6,subQ5,subQ4,subQ3,subQ2,subQ1,subQ0])],"isStart":true}),makeQuery(id+"F3.opExtrude","CAP_FACE",FACE,{"disambiguationData":[OSD([subQ17,subQ16,subQ15,subQ14,subQ13,subQ12,subQ11,subQ10,subQ9,subQ8,subQ7,subQ6,subQ5,subQ4,subQ3,subQ2,subQ1,subQ0])],"isStart":false})]});}
            var sketch = newSketch(context, id + "F8", { "sketchPlane" : qUnion([Q0])});
            skLineSegment(sketch, "E34.bottom", {"start": v(-32.79, 33.4) * mm, "end": v(56.11, 33.4) * mm});
            skLineSegment(sketch, "E34.top", {"start": v(-32.79, -29.95) * mm, "end": v(56.11, -29.95) * mm});
            skLineSegment(sketch, "E34.left", {"start": v(-32.79, 33.4) * mm, "end": v(-32.79, -29.95) * mm});
            skLineSegment(sketch, "E34.right", {"start": v(56.11, 33.4) * mm, "end": v(56.11, -29.95) * mm});
            skLineSegment(sketch, "E35.0.0", {"start": v(49.76, 33.4) * mm, "end": v(-26.44, 33.4) * mm});
            skLineSegment(sketch, "E35.0.1", {"start": v(-26.44, 33.4) * mm, "end": v(-26.44, -29.95) * mm});
            skLineSegment(sketch, "E35.0.2", {"start": v(-26.44, -29.95) * mm, "end": v(49.76, -29.95) * mm});
            skLineSegment(sketch, "E35.0.3", {"start": v(49.76, -29.95) * mm, "end": v(49.76, 33.4) * mm});
            skSolve(sketch);
        }
        {
            var Q0;
            {var subQ2=sQuery(id+"F8.wireOp",EDGE,"E34.left");Q0=makeQuery(id+"F8.imprint","IMPRINT",FACE,{"disambiguationData":[TD([[makeQuery(id+"F8.imprint","IMPRINT",EDGE,{"derivedFrom":subQ2}),1.0]])]});}
            var Q1;
            {var subQ2=sQuery(id+"F8.wireOp",EDGE,"E34.right");Q1=makeQuery(id+"F8.imprint","IMPRINT",FACE,{"disambiguationData":[TD([[makeQuery(id+"F8.imprint","IMPRINT",EDGE,{"derivedFrom":subQ2}),-1.0]])]});}
            var Q2;
            Q2=makeQuery(id+"F7.opExtrude","CAP_FACE",FACE,{"disambiguationData":[OSD([sQuery(id+"F6.wireOp",EDGE,"E32")])],"isStart":false});
            extrude(context, id + "F9", {"entities" : qUnion([Q0, Q1]), "operationType" : NewBodyOperationType.ADD, "endBound" : BoundingType.UP_TO_SURFACE, "oppositeDirection" : true, "endBoundEntityFace" : qUnion([Q2]), "depth" : 12.7 * mm});
        }
        {
            var Q0;
            Q0=makeQuery(id+"F9.opExtrude","SWEPT_FACE",FACE,{"disambiguationData":[OSD([sQuery(id+"F8.wireOp",EDGE,"E34.left")])]});
            var sketch = newSketch(context, id + "F10", { "sketchPlane" : qUnion([Q0])});
            skCircle(sketch, "E36", {"center": v(1.73, -50.8) * mm, "radius": 10 * mm});
            skLineSegment(sketch, "E37.0.0", {"start": v(33.4, 0) * mm, "end": v(33.4, 14.1) * mm});
            skLineSegment(sketch, "E37.0.1", {"start": v(33.4, 14.1) * mm, "end": v(-29.95, 14.1) * mm});
            skLineSegment(sketch, "E37.0.2", {"start": v(-29.95, 14.1) * mm, "end": v(-29.95, 0) * mm});
            skLineSegment(sketch, "E37.0.3", {"start": v(-29.95, 0) * mm, "end": v(33.4, 0) * mm});
            skLineSegment(sketch, "E38", {"start": v(-7.52, -54.6) * mm, "end": v(10.98, -54.6) * mm});
            skLineSegment(sketch, "E39", {"start": v(10.98, -54.6) * mm, "end": v(33.4, 0) * mm});
            skLineSegment(sketch, "E40", {"start": v(-7.52, -54.6) * mm, "end": v(-29.95, 0) * mm});
            skLineSegment(sketch, "E41", {"start": v(20.7, 0) * mm, "end": v(-17.25, 0) * mm});
            skLineSegment(sketch, "E42", {"start": v(20.7, 0) * mm, "end": v(3.85, -41.03) * mm});
            skLineSegment(sketch, "E43", {"start": v(-17.25, 0) * mm, "end": v(-0.4, -41.03) * mm});
            skSolve(sketch);
        }
        {
            var Q0;
            Q0 = qSketchRegion(id + "F10", true);
            extrude(context, id + "F11", {"entities" : qUnion([Q0]), "operationType" : NewBodyOperationType.ADD, "depth" : 6.35 * mm});
        }
        {
            var Q0;
            Q0=makeQuery(id+"F9.opExtrude","SWEPT_FACE",FACE,{"disambiguationData":[OSD([sQuery(id+"F8.wireOp",EDGE,"E34.right")])]});
            var sketch = newSketch(context, id + "F12", { "sketchPlane" : qUnion([Q0])});
            skLineSegment(sketch, "E44.0.0", {"start": v(29.95, 14.1) * mm, "end": v(-33.4, 14.1) * mm});
            skLineSegment(sketch, "E44.0.1", {"start": v(-33.4, 14.1) * mm, "end": v(-33.4, 0) * mm});
            skLineSegment(sketch, "E44.0.2", {"start": v(-33.4, 0) * mm, "end": v(29.95, 0) * mm});
            skLineSegment(sketch, "E44.0.3", {"start": v(29.95, 0) * mm, "end": v(29.95, 14.1) * mm});
            skLineSegment(sketch, "E45.0.0", {"start": v(-20.7, 0) * mm, "end": v(-33.4, 0) * mm});
            skLineSegment(sketch, "E45.0.1", {"start": v(-33.4, 0) * mm, "end": v(-10.98, -54.6) * mm});
            skArc(sketch, "E45.0.2", {"start": v(-10.98, -54.6) * mm, "mid": v(-1.73, -60.8) * mm, "end": v(7.52, -54.6) * mm});
            skLineSegment(sketch, "E45.0.3", {"start": v(7.52, -54.6) * mm, "end": v(29.95, 0) * mm});
            skLineSegment(sketch, "E45.0.4", {"start": v(29.95, 0) * mm, "end": v(17.25, 0) * mm});
            skLineSegment(sketch, "E45.0.5", {"start": v(17.25, 0) * mm, "end": v(0.4, -41.03) * mm});
            skArc(sketch, "E45.0.6", {"start": v(0.4, -41.03) * mm, "mid": v(-1.73, -40.8) * mm, "end": v(-3.85, -41.03) * mm});
            skLineSegment(sketch, "E45.0.7", {"start": v(-3.85, -41.03) * mm, "end": v(-20.7, 0) * mm});
            skSolve(sketch);
        }
        {
            var Q0;
            Q0 = qSketchRegion(id + "F12", true);
            extrude(context, id + "F13", {"entities" : qUnion([Q0]), "operationType" : NewBodyOperationType.ADD, "depth" : 6.35 * mm});
        }
        {
            var Q0;
            Q0=makeQuery(id+"F13.opExtrude","CAP_FACE",FACE,{"disambiguationData":[OSD([sQuery(id+"F12.wireOp",EDGE,"E44.0.0"),sQuery(id+"F12.wireOp",EDGE,"E44.0.1"),sQuery(id+"F12.wireOp",EDGE,"E44.0.2"),sQuery(id+"F12.wireOp",EDGE,"E44.0.3"),sQuery(id+"F12.wireOp",EDGE,"E45.0.1"),sQuery(id+"F12.wireOp",EDGE,"E45.0.2"),sQuery(id+"F12.wireOp",EDGE,"E45.0.3"),sQuery(id+"F12.wireOp",EDGE,"E45.0.5"),sQuery(id+"F12.wireOp",EDGE,"E45.0.6"),sQuery(id+"F12.wireOp",EDGE,"E45.0.7")])],"isStart":true});
            var sketch = newSketch(context, id + "F14", { "sketchPlane" : qUnion([Q0])});
            skLineSegment(sketch, "E46.0.0", {"start": v(10.98, -54.6) * mm, "end": v(33.4, 0) * mm});
            skLineSegment(sketch, "E46.0.1", {"start": v(33.4, 0) * mm, "end": v(20.7, 0) * mm});
            skLineSegment(sketch, "E46.0.2", {"start": v(20.7, 0) * mm, "end": v(3.85, -41.03) * mm});
            skArc(sketch, "E46.0.3", {"start": v(3.85, -41.03) * mm, "mid": v(1.73, -40.8) * mm, "end": v(-0.4, -41.03) * mm});
            skLineSegment(sketch, "E46.0.4", {"start": v(-0.4, -41.03) * mm, "end": v(-17.25, 0) * mm});
            skLineSegment(sketch, "E46.0.5", {"start": v(-17.25, 0) * mm, "end": v(-29.95, 0) * mm});
            skLineSegment(sketch, "E46.0.6", {"start": v(-29.95, 0) * mm, "end": v(-7.52, -54.6) * mm});
            skArc(sketch, "E46.0.7", {"start": v(-7.52, -54.6) * mm, "mid": v(1.73, -60.8) * mm, "end": v(10.98, -54.6) * mm});
            skCircle(sketch, "E47", {"center": v(1.73, -50.8) * mm, "radius": 10 * mm});
            skSolve(sketch);
        }
        {
            var Q0;
            {var subQ0=sQuery(id+"F14.wireOp",EDGE,"E47");var subQ1=makeQuery(id+"F14.imprint","INTERSECT",VERTEX,{"derivedFrom":[sQuery(id+"F14.wireOp",EDGE,"E46.0.4"),subQ0]});var subQ2=makeQuery(id+"F14.imprint","INTERSECT",VERTEX,{"derivedFrom":[sQuery(id+"F14.wireOp",EDGE,"E46.0.2"),subQ0]});Q0=makeQuery(id+"F14.imprint","IMPRINT",FACE,{"disambiguationData":[TD([[makeQuery(id+"F14.imprint","IMPRINT",EDGE,{"disambiguationData":[TD([[subQ1,-1.0],[subQ2,1.0]])],"derivedFrom":subQ0}),-1.0]])]});}
            extrude(context, id + "F15", {"entities" : qUnion([Q0]), "operationType" : NewBodyOperationType.ADD, "endBound" : BoundingType.UP_TO_NEXT, "depth" : 25.4 * mm});
        }
        {
            var Q0;
            Q0=makeQuery(id+"F13.opExtrude","CAP_FACE",FACE,{"disambiguationData":[OSD([sQuery(id+"F12.wireOp",EDGE,"E44.0.0"),sQuery(id+"F12.wireOp",EDGE,"E44.0.1"),sQuery(id+"F12.wireOp",EDGE,"E44.0.2"),sQuery(id+"F12.wireOp",EDGE,"E44.0.3"),sQuery(id+"F12.wireOp",EDGE,"E45.0.1"),sQuery(id+"F12.wireOp",EDGE,"E45.0.2"),sQuery(id+"F12.wireOp",EDGE,"E45.0.3"),sQuery(id+"F12.wireOp",EDGE,"E45.0.5"),sQuery(id+"F12.wireOp",EDGE,"E45.0.6"),sQuery(id+"F12.wireOp",EDGE,"E45.0.7")])],"isStart":false});
            var sketch = newSketch(context, id + "F16", { "sketchPlane" : qUnion([Q0])});
            skLineSegment(sketch, "E48.0.0", {"start": v(29.95, 14.1) * mm, "end": v(-33.4, 14.1) * mm});
            skLineSegment(sketch, "E48.0.1", {"start": v(-33.4, 14.1) * mm, "end": v(-33.4, 0) * mm});
            skLineSegment(sketch, "E48.0.2", {"start": v(-33.4, 0) * mm, "end": v(-10.98, -54.6) * mm});
            skArc(sketch, "E48.0.3", {"start": v(-10.98, -54.6) * mm, "mid": v(-1.73, -60.8) * mm, "end": v(7.52, -54.6) * mm});
            skLineSegment(sketch, "E48.0.4", {"start": v(7.52, -54.6) * mm, "end": v(29.95, 0) * mm});
            skLineSegment(sketch, "E48.0.5", {"start": v(29.95, 0) * mm, "end": v(29.95, 14.1) * mm});
            skCircle(sketch, "E49", {"center": v(-1.73, -50.8) * mm, "radius": 5 * mm});
            skSolve(sketch);
        }
        {
            var Q0;
            Q0=makeQuery(id+"F16.imprint","IMPRINT",FACE,{"disambiguationData":[TD([[makeQuery(id+"F16.imprint","IMPRINT",EDGE,{"derivedFrom":sQuery(id+"F16.wireOp",EDGE,"E49")}),1.0]])]});
            extrude(context, id + "F17", {"entities" : qUnion([Q0]), "operationType" : NewBodyOperationType.REMOVE, "endBound" : BoundingType.THROUGH_ALL, "oppositeDirection" : true, "depth" : 25.4 * mm});
        }
        {
            var Q0;
            Q0=makeQuery(id+"F11.opExtrude","CAP_FACE",FACE,{"disambiguationData":[OSD([sQuery(id+"F10.wireOp",EDGE,"E36"),sQuery(id+"F10.wireOp",EDGE,"E37.0.0"),sQuery(id+"F10.wireOp",EDGE,"E37.0.1"),sQuery(id+"F10.wireOp",EDGE,"E37.0.2"),sQuery(id+"F10.wireOp",EDGE,"E39"),sQuery(id+"F10.wireOp",EDGE,"E40"),sQuery(id+"F10.wireOp",EDGE,"E41"),sQuery(id+"F10.wireOp",EDGE,"E42"),sQuery(id+"F10.wireOp",EDGE,"E43")])],"isStart":false});
            var sketch = newSketch(context, id + "F18", { "sketchPlane" : qUnion([Q0])});
            skCircle(sketch, "E50.0", {"center": v(1.73, -50.8) * mm, "radius": 5 * mm});
            skCircle(sketch, "E51", {"center": v(1.73, -50.8) * mm, "radius": 3.5 * mm});
            skSolve(sketch);
        }
        {
            var Q0;
            Q0=makeQuery(id+"F18.imprint","IMPRINT",FACE,{"disambiguationData":[TD([[makeQuery(id+"F18.imprint","IMPRINT",EDGE,{"derivedFrom":sQuery(id+"F18.wireOp",EDGE,"E50.0")}),1.0]])]});
            extrude(context, id + "F19", {"entities" : qUnion([Q0]), "operationType" : NewBodyOperationType.ADD, "oppositeDirection" : true, "depth" : 4 * mm});
        }
        {
            var Q0;
            {var subQ0=sQuery(id+"F10.wireOp",EDGE,"E37.0.0");var subQ19=sQuery(id+"F10.wireOp",EDGE,"E42");var subQ20=sQuery(id+"F10.wireOp",EDGE,"E36");var subQ21=sQuery(id+"F10.wireOp",EDGE,"E43");var subQ29=sQuery(id+"F10.wireOp",EDGE,"E40");var subQ31=sQuery(id+"F10.wireOp",EDGE,"E39");var subQ32=sQuery(id+"F10.wireOp",EDGE,"E41");Q0=makeQuery(id+"F15.boolean.opBoolean","SPLIT",FACE,{"disambiguationData":[TD([makeQuery(id+"F3.opExtrude","SWEPT_FACE",FACE,{"disambiguationData":[OSD([sQuery(id+"F2.wireOp",EDGE,"E17.top")])]})])],"derivedFrom":makeQuery(id+"F11.opExtrude","CAP_FACE",FACE,{"disambiguationData":[OSD([subQ20,subQ0,sQuery(id+"F10.wireOp",EDGE,"E37.0.1"),sQuery(id+"F10.wireOp",EDGE,"E37.0.2"),subQ31,subQ29,subQ32,subQ19,subQ21])],"isStart":true})});}
            var sketch = newSketch(context, id + "F20", { "sketchPlane" : qUnion([Q0])});
            skArc(sketch, "E52.0.0", {"start": v(-3.85, -41.03) * mm, "mid": v(-10.58, -46.15) * mm, "end": v(-10.98, -54.6) * mm});
            skLineSegment(sketch, "E52.0.1", {"start": v(-3.85, -41.03) * mm, "end": v(-20.7, 0) * mm});
            skLineSegment(sketch, "E52.0.2", {"start": v(-20.7, 0) * mm, "end": v(-33.4, 0) * mm});
            skLineSegment(sketch, "E52.0.3", {"start": v(-33.4, 0) * mm, "end": v(-10.98, -54.6) * mm});
            skArc(sketch, "E53.0.0", {"start": v(7.52, -54.6) * mm, "mid": v(7.13, -46.15) * mm, "end": v(0.4, -41.03) * mm});
            skLineSegment(sketch, "E53.0.1", {"start": v(7.52, -54.6) * mm, "end": v(29.95, 0) * mm});
            skLineSegment(sketch, "E53.0.2", {"start": v(29.95, 0) * mm, "end": v(17.25, 0) * mm});
            skLineSegment(sketch, "E53.0.3", {"start": v(17.25, 0) * mm, "end": v(0.4, -41.03) * mm});
            skSolve(sketch);
        }
        {
            var Q0;
            Q0 = qSketchRegion(id + "F20", true);
            extrude(context, id + "F21", {"entities" : qUnion([Q0]), "operationType" : NewBodyOperationType.ADD, "depth" : 3.17 * mm});
        }
        {
            var Q0;
            {var subQ5=sQuery(id+"F12.wireOp",EDGE,"E45.0.2");var subQ9=sQuery(id+"F0.wireOp",EDGE,"E0.bottom");var subQ27=sQuery(id+"F12.wireOp",EDGE,"E45.0.5");var subQ29=sQuery(id+"F12.wireOp",EDGE,"E45.0.3");var subQ30=sQuery(id+"F12.wireOp",EDGE,"E44.0.2");var subQ31=sQuery(id+"F12.wireOp",EDGE,"E44.0.3");var subQ32=sQuery(id+"F12.wireOp",EDGE,"E45.0.6");Q0=makeQuery(id+"F15.boolean.opBoolean","SPLIT",FACE,{"disambiguationData":[TD([makeQuery(id+"F1.opExtrude","SWEPT_FACE",FACE,{"disambiguationData":[OSD([subQ9])]})])],"derivedFrom":makeQuery(id+"F13.opExtrude","CAP_FACE",FACE,{"disambiguationData":[OSD([sQuery(id+"F12.wireOp",EDGE,"E44.0.0"),sQuery(id+"F12.wireOp",EDGE,"E44.0.1"),subQ30,subQ31,sQuery(id+"F12.wireOp",EDGE,"E45.0.1"),subQ5,subQ29,subQ27,subQ32,sQuery(id+"F12.wireOp",EDGE,"E45.0.7")])],"isStart":true})});}
            var sketch = newSketch(context, id + "F22", { "sketchPlane" : qUnion([Q0])});
            skLineSegment(sketch, "E54.0.0", {"start": v(20.7, 0) * mm, "end": v(3.85, -41.03) * mm});
            skArc(sketch, "E54.0.1", {"start": v(3.85, -41.03) * mm, "mid": v(10.58, -46.15) * mm, "end": v(10.98, -54.6) * mm});
            skLineSegment(sketch, "E54.0.2", {"start": v(10.98, -54.6) * mm, "end": v(33.4, 0) * mm});
            skLineSegment(sketch, "E54.0.3", {"start": v(33.4, 0) * mm, "end": v(20.7, 0) * mm});
            skLineSegment(sketch, "E55.0.0", {"start": v(-29.95, 0) * mm, "end": v(-7.52, -54.6) * mm});
            skArc(sketch, "E55.0.1", {"start": v(-7.52, -54.6) * mm, "mid": v(-7.13, -46.15) * mm, "end": v(-0.4, -41.03) * mm});
            skLineSegment(sketch, "E55.0.2", {"start": v(-0.4, -41.03) * mm, "end": v(-17.25, 0) * mm});
            skLineSegment(sketch, "E55.0.3", {"start": v(-17.25, 0) * mm, "end": v(-29.95, 0) * mm});
            skSolve(sketch);
        }
        {
            var Q0;
            Q0 = qSketchRegion(id + "F22", true);
            extrude(context, id + "F23", {"entities" : qUnion([Q0]), "operationType" : NewBodyOperationType.ADD, "depth" : 3.17 * mm});
        }
        {
            var Q0;
            Q0=makeQuery(id+"F9.opExtrude","SWEPT_FACE",FACE,{"disambiguationData":[OSD([sQuery(id+"F8.wireOp",EDGE,"E35.0.1")])]});
            var sketch = newSketch(context, id + "F24", { "sketchPlane" : qUnion([Q0])});
            skLineSegment(sketch, "E56.0.0", {"start": v(-33.4, 6.35) * mm, "end": v(29.95, 6.35) * mm});
            skLineSegment(sketch, "E56.0.1", {"start": v(29.95, 6.35) * mm, "end": v(29.95, 14.1) * mm});
            skLineSegment(sketch, "E56.0.2", {"start": v(29.95, 14.1) * mm, "end": v(-33.4, 14.1) * mm});
            skLineSegment(sketch, "E56.0.3", {"start": v(-33.4, 14.1) * mm, "end": v(-33.4, 6.35) * mm});
            skSolve(sketch);
        }
        {
            var Q0;
            Q0 = qSketchRegion(id + "F24", true);
            extrude(context, id + "F25", {"entities" : qUnion([Q0]), "operationType" : NewBodyOperationType.REMOVE, "oppositeDirection" : true, "depth" : 1.27 * mm});
        }
        {
            var Q0;
            Q0=makeQuery(id+"F9.opExtrude","SWEPT_FACE",FACE,{"disambiguationData":[OSD([sQuery(id+"F8.wireOp",EDGE,"E35.0.3")])]});
            var sketch = newSketch(context, id + "F26", { "sketchPlane" : qUnion([Q0])});
            skLineSegment(sketch, "E57.0.0", {"start": v(-29.95, 14.1) * mm, "end": v(-29.95, 6.35) * mm});
            skLineSegment(sketch, "E57.0.1", {"start": v(-29.95, 6.35) * mm, "end": v(33.4, 6.35) * mm});
            skLineSegment(sketch, "E57.0.2", {"start": v(33.4, 6.35) * mm, "end": v(33.4, 14.1) * mm});
            skLineSegment(sketch, "E57.0.3", {"start": v(33.4, 14.1) * mm, "end": v(-29.95, 14.1) * mm});
            skSolve(sketch);
        }
        {
            var Q0;
            Q0 = qSketchRegion(id + "F26", true);
            extrude(context, id + "F27", {"entities" : qUnion([Q0]), "operationType" : NewBodyOperationType.REMOVE, "oppositeDirection" : true, "depth" : 1.27 * mm});
        }
        {
            var Q0;
            Q0=makeQuery(id+"F11.opExtrude","CAP_EDGE",EDGE,{"disambiguationData":[OSD([sQuery(id+"F10.wireOp",EDGE,"E37.0.1")])],"isStart":false});
            var Q1;
            Q1=makeQuery(id+"F13.opExtrude","CAP_EDGE",EDGE,{"disambiguationData":[OSD([sQuery(id+"F12.wireOp",EDGE,"E44.0.0")])],"isStart":false});
            var Q2;
            {var subQ0=sQuery(id+"F8.wireOp",EDGE,"E34.top");Q2=makeQuery(id+"F13.boolean.opBoolean","MERGE",EDGE,{"derivedFrom":[makeQuery(id+"F9.opExtrude","TWEAK_EDGE",EDGE,{"derivedFrom":[makeQuery(id+"F7.opExtrude","CAP_FACE",FACE,{"disambiguationData":[OSD([sQuery(id+"F6.wireOp",EDGE,"E32")])],"isStart":false}),makeQuery(id+"F8.imprint","IMPRINT",EDGE,{"disambiguationData":[TD([[makeQuery(id+"F8.imprint","INTERSECT",VERTEX,{"derivedFrom":[subQ0,sQuery(id+"F8.wireOp",EDGE,"E34.right")]}),1.0]])],"derivedFrom":subQ0})]}),makeQuery(id+"F13.opExtrude","SWEPT_EDGE",EDGE,{"disambiguationData":[OSD([sQuery(id+"F12.wireOp",EDGE,"E44.0.0"),sQuery(id+"F12.wireOp",EDGE,"E44.0.3")])]})]});}
            var Q3;
            {var subQ0=sQuery(id+"F8.wireOp",EDGE,"E34.top");Q3=makeQuery(id+"F11.boolean.opBoolean","MERGE",EDGE,{"derivedFrom":[makeQuery(id+"F9.opExtrude","TWEAK_EDGE",EDGE,{"derivedFrom":[makeQuery(id+"F7.opExtrude","CAP_FACE",FACE,{"disambiguationData":[OSD([sQuery(id+"F6.wireOp",EDGE,"E32")])],"isStart":false}),makeQuery(id+"F8.imprint","IMPRINT",EDGE,{"disambiguationData":[TD([[makeQuery(id+"F8.imprint","INTERSECT",VERTEX,{"derivedFrom":[subQ0,sQuery(id+"F8.wireOp",EDGE,"E34.left")]}),-1.0]])],"derivedFrom":subQ0})]}),makeQuery(id+"F11.opExtrude","SWEPT_EDGE",EDGE,{"disambiguationData":[OSD([sQuery(id+"F10.wireOp",EDGE,"E37.0.1"),sQuery(id+"F10.wireOp",EDGE,"E37.0.2")])]})]});}
            var Q4;
            {var subQ0=sQuery(id+"F8.wireOp",EDGE,"E34.bottom");Q4=makeQuery(id+"F11.boolean.opBoolean","MERGE",EDGE,{"derivedFrom":[makeQuery(id+"F9.opExtrude","TWEAK_EDGE",EDGE,{"derivedFrom":[makeQuery(id+"F7.opExtrude","CAP_FACE",FACE,{"disambiguationData":[OSD([sQuery(id+"F6.wireOp",EDGE,"E32")])],"isStart":false}),makeQuery(id+"F8.imprint","IMPRINT",EDGE,{"disambiguationData":[TD([[makeQuery(id+"F8.imprint","INTERSECT",VERTEX,{"derivedFrom":[subQ0,sQuery(id+"F8.wireOp",EDGE,"E34.left")]}),-1.0]])],"derivedFrom":subQ0})]}),makeQuery(id+"F11.opExtrude","SWEPT_EDGE",EDGE,{"disambiguationData":[OSD([sQuery(id+"F10.wireOp",EDGE,"E37.0.0"),sQuery(id+"F10.wireOp",EDGE,"E37.0.1")])]})]});}
            var Q5;
            {var subQ0=sQuery(id+"F8.wireOp",EDGE,"E34.bottom");Q5=makeQuery(id+"F13.boolean.opBoolean","MERGE",EDGE,{"derivedFrom":[makeQuery(id+"F9.opExtrude","TWEAK_EDGE",EDGE,{"derivedFrom":[makeQuery(id+"F7.opExtrude","CAP_FACE",FACE,{"disambiguationData":[OSD([sQuery(id+"F6.wireOp",EDGE,"E32")])],"isStart":false}),makeQuery(id+"F8.imprint","IMPRINT",EDGE,{"disambiguationData":[TD([[makeQuery(id+"F8.imprint","INTERSECT",VERTEX,{"derivedFrom":[subQ0,sQuery(id+"F8.wireOp",EDGE,"E34.right")]}),1.0]])],"derivedFrom":subQ0})]}),makeQuery(id+"F13.opExtrude","SWEPT_EDGE",EDGE,{"disambiguationData":[OSD([sQuery(id+"F12.wireOp",EDGE,"E44.0.0"),sQuery(id+"F12.wireOp",EDGE,"E44.0.1")])]})]});}
            var Q6;
            Q6=makeQuery(id+"F11.opExtrude","CAP_EDGE",EDGE,{"disambiguationData":[OSD([sQuery(id+"F10.wireOp",EDGE,"E37.0.0")])],"isStart":false});
            var Q7;
            Q7=makeQuery(id+"F11.opExtrude","CAP_EDGE",EDGE,{"disambiguationData":[OSD([sQuery(id+"F10.wireOp",EDGE,"E37.0.2")])],"isStart":false});
            var Q8;
            Q8=makeQuery(id+"F13.opExtrude","CAP_EDGE",EDGE,{"disambiguationData":[OSD([sQuery(id+"F12.wireOp",EDGE,"E44.0.1")])],"isStart":false});
            var Q9;
            Q9=makeQuery(id+"F13.opExtrude","CAP_EDGE",EDGE,{"disambiguationData":[OSD([sQuery(id+"F12.wireOp",EDGE,"E44.0.3")])],"isStart":false});
            var Q10;
            Q10=makeQuery(id+"F13.opExtrude","CAP_EDGE",EDGE,{"disambiguationData":[OSD([sQuery(id+"F12.wireOp",EDGE,"E45.0.3")])],"isStart":false});
            var Q11;
            Q11=makeQuery(id+"F13.opExtrude","CAP_EDGE",EDGE,{"disambiguationData":[OSD([sQuery(id+"F12.wireOp",EDGE,"E45.0.1")])],"isStart":false});
            var Q12;
            Q12=makeQuery(id+"F11.opExtrude","CAP_EDGE",EDGE,{"disambiguationData":[OSD([sQuery(id+"F10.wireOp",EDGE,"E40")])],"isStart":false});
            var Q13;
            Q13=makeQuery(id+"F13.opExtrude","CAP_EDGE",EDGE,{"disambiguationData":[OSD([sQuery(id+"F12.wireOp",EDGE,"E45.0.7")])],"isStart":false});
            var Q14;
            Q14=makeQuery(id+"F13.opExtrude","CAP_EDGE",EDGE,{"disambiguationData":[OSD([sQuery(id+"F12.wireOp",EDGE,"E45.0.6")])],"isStart":false});
            var Q15;
            Q15=makeQuery(id+"F13.opExtrude","CAP_EDGE",EDGE,{"disambiguationData":[OSD([sQuery(id+"F12.wireOp",EDGE,"E45.0.5")])],"isStart":false});
            var Q16;
            Q16=makeQuery(id+"F13.opExtrude","CAP_EDGE",EDGE,{"disambiguationData":[OSD([sQuery(id+"F12.wireOp",EDGE,"E44.0.2")])],"isStart":false});
            var Q17;
            {var subQ0=sQuery(id+"F10.wireOp",EDGE,"E36");Q17=makeQuery(id+"F11.opExtrude","CAP_EDGE",EDGE,{"disambiguationData":[OSD([subQ0]),TDD([makeQuery(id+"F10.imprint","IMPRINT",EDGE,{"disambiguationData":[TD([[makeQuery(id+"F10.imprint","INTERSECT",VERTEX,{"derivedFrom":[subQ0,sQuery(id+"F10.wireOp",EDGE,"E42")]}),-1.0]])],"derivedFrom":subQ0})])],"isStart":false});}
            var Q18;
            Q18=makeQuery(id+"F11.opExtrude","CAP_EDGE",EDGE,{"disambiguationData":[OSD([sQuery(id+"F10.wireOp",EDGE,"E43")])],"isStart":false});
            var Q19;
            Q19=makeQuery(id+"F11.opExtrude","CAP_EDGE",EDGE,{"disambiguationData":[OSD([sQuery(id+"F10.wireOp",EDGE,"E42")])],"isStart":false});
            var Q20;
            Q20=makeQuery(id+"F11.opExtrude","CAP_EDGE",EDGE,{"disambiguationData":[OSD([sQuery(id+"F10.wireOp",EDGE,"E41")])],"isStart":false});
            var Q21;
            {var subQ19=sQuery(id+"F8.wireOp",EDGE,"E34.right");Q21=makeQuery(id+"F13.boolean.opBoolean","SPLIT",EDGE,{"disambiguationData":[TD([makeQuery(id+"F3.opExtrude","SWEPT_FACE",FACE,{"disambiguationData":[OSD([sQuery(id+"F2.wireOp",EDGE,"E17.top")])]})])],"derivedFrom":makeQuery(id+"F9.opExtrude","CAP_EDGE",EDGE,{"disambiguationData":[OSD([subQ19])],"isStart":true})});}
            var Q22;
            {var subQ4=sQuery(id+"F8.wireOp",EDGE,"E34.right");var subQ8=sQuery(id+"F0.wireOp",EDGE,"E0.bottom");Q22=makeQuery(id+"F13.boolean.opBoolean","SPLIT",EDGE,{"disambiguationData":[TD([makeQuery(id+"F1.opExtrude","SWEPT_FACE",FACE,{"disambiguationData":[OSD([subQ8])]})])],"derivedFrom":makeQuery(id+"F9.opExtrude","CAP_EDGE",EDGE,{"disambiguationData":[OSD([subQ4])],"isStart":true})});}
            var Q23;
            {var subQ4=sQuery(id+"F0.wireOp",EDGE,"E0.bottom");var subQ28=sQuery(id+"F8.wireOp",EDGE,"E34.left");Q23=makeQuery(id+"F11.boolean.opBoolean","SPLIT",EDGE,{"disambiguationData":[TD([makeQuery(id+"F1.opExtrude","SWEPT_FACE",FACE,{"disambiguationData":[OSD([subQ4])]})])],"derivedFrom":makeQuery(id+"F9.opExtrude","CAP_EDGE",EDGE,{"disambiguationData":[OSD([subQ28])],"isStart":true})});}
            var Q24;
            {var subQ28=sQuery(id+"F8.wireOp",EDGE,"E34.left");Q24=makeQuery(id+"F11.boolean.opBoolean","SPLIT",EDGE,{"disambiguationData":[TD([makeQuery(id+"F3.opExtrude","SWEPT_FACE",FACE,{"disambiguationData":[OSD([sQuery(id+"F2.wireOp",EDGE,"E17.top")])]})])],"derivedFrom":makeQuery(id+"F9.opExtrude","CAP_EDGE",EDGE,{"disambiguationData":[OSD([subQ28])],"isStart":true})});}
            var Q25;
            {var subQ0=sQuery(id+"F10.wireOp",EDGE,"E40");var subQ2=sQuery(id+"F10.wireOp",EDGE,"E36");Q25=makeQuery(id+"F15.boolean.opBoolean","SPLIT",EDGE,{"disambiguationData":[TD([makeQuery(id+"F11.opExtrude","SWEPT_FACE",FACE,{"disambiguationData":[OSD([subQ0])]})])],"derivedFrom":makeQuery(id+"F15.opExtrude","CAP_EDGE",EDGE,{"disambiguationData":[OSD([subQ2])],"isStart":false})});}
            var Q26;
            {var subQ0=sQuery(id+"F10.wireOp",EDGE,"E39");var subQ3=sQuery(id+"F10.wireOp",EDGE,"E36");Q26=makeQuery(id+"F15.boolean.opBoolean","SPLIT",EDGE,{"disambiguationData":[TD([makeQuery(id+"F11.opExtrude","SWEPT_FACE",FACE,{"disambiguationData":[OSD([subQ0])]})])],"derivedFrom":makeQuery(id+"F15.opExtrude","CAP_EDGE",EDGE,{"disambiguationData":[OSD([subQ3])],"isStart":false})});}
            var Q27;
            {var subQ0=sQuery(id+"F12.wireOp",EDGE,"E45.0.1");var subQ6=sQuery(id+"F14.wireOp",EDGE,"E47");Q27=makeQuery(id+"F15.boolean.opBoolean","SPLIT",EDGE,{"disambiguationData":[TD([makeQuery(id+"F13.opExtrude","SWEPT_FACE",FACE,{"disambiguationData":[OSD([subQ0])]})])],"derivedFrom":makeQuery(id+"F15.opExtrude","CAP_EDGE",EDGE,{"disambiguationData":[OSD([subQ6])],"isStart":true})});}
            var Q28;
            {var subQ2=sQuery(id+"F12.wireOp",EDGE,"E45.0.3");var subQ6=sQuery(id+"F14.wireOp",EDGE,"E47");Q28=makeQuery(id+"F15.boolean.opBoolean","SPLIT",EDGE,{"disambiguationData":[TD([makeQuery(id+"F13.opExtrude","SWEPT_FACE",FACE,{"disambiguationData":[OSD([subQ2])]})])],"derivedFrom":makeQuery(id+"F15.opExtrude","CAP_EDGE",EDGE,{"disambiguationData":[OSD([subQ6])],"isStart":true})});}
            var Q29;
            Q29=makeQuery(id+"F21.opExtrude","CAP_EDGE",EDGE,{"disambiguationData":[OSD([sQuery(id+"F20.wireOp",EDGE,"E53.0.2")])],"isStart":false});
            var Q30;
            Q30=makeQuery(id+"F21.opExtrude","CAP_EDGE",EDGE,{"disambiguationData":[OSD([sQuery(id+"F20.wireOp",EDGE,"E52.0.2")])],"isStart":false});
            var Q31;
            Q31=makeQuery(id+"F21.opExtrude","CAP_EDGE",EDGE,{"disambiguationData":[OSD([sQuery(id+"F20.wireOp",EDGE,"E53.0.0")])],"isStart":false});
            var Q32;
            Q32=makeQuery(id+"F21.opExtrude","CAP_EDGE",EDGE,{"disambiguationData":[OSD([sQuery(id+"F20.wireOp",EDGE,"E52.0.0")])],"isStart":false});
            var Q33;
            Q33=makeQuery(id+"F23.opExtrude","CAP_EDGE",EDGE,{"disambiguationData":[OSD([sQuery(id+"F22.wireOp",EDGE,"E54.0.3")])],"isStart":false});
            var Q34;
            Q34=makeQuery(id+"F23.opExtrude","CAP_EDGE",EDGE,{"disambiguationData":[OSD([sQuery(id+"F22.wireOp",EDGE,"E55.0.3")])],"isStart":false});
            var Q35;
            Q35=makeQuery(id+"F23.opExtrude","CAP_EDGE",EDGE,{"disambiguationData":[OSD([sQuery(id+"F22.wireOp",EDGE,"E54.0.1")])],"isStart":false});
            var Q36;
            Q36=makeQuery(id+"F23.opExtrude","CAP_EDGE",EDGE,{"disambiguationData":[OSD([sQuery(id+"F22.wireOp",EDGE,"E55.0.1")])],"isStart":false});
            fillet(context, id + "F28", {"entities" : qUnion([Q0, Q1, Q2, Q3, Q4, Q5, Q6, Q7, Q8, Q9, Q10, Q11, Q12, Q13, Q14, Q15, Q16, Q17, Q18, Q19, Q20, Q21, Q22, Q23, Q24, Q25, Q26, Q27, Q28, Q29, Q30, Q31, Q32, Q33, Q34, Q35, Q36]), "radius" : 5.08 * mm, "tangentPropagation" : true, "allowEdgeOverflow" : false});
        }
    });
